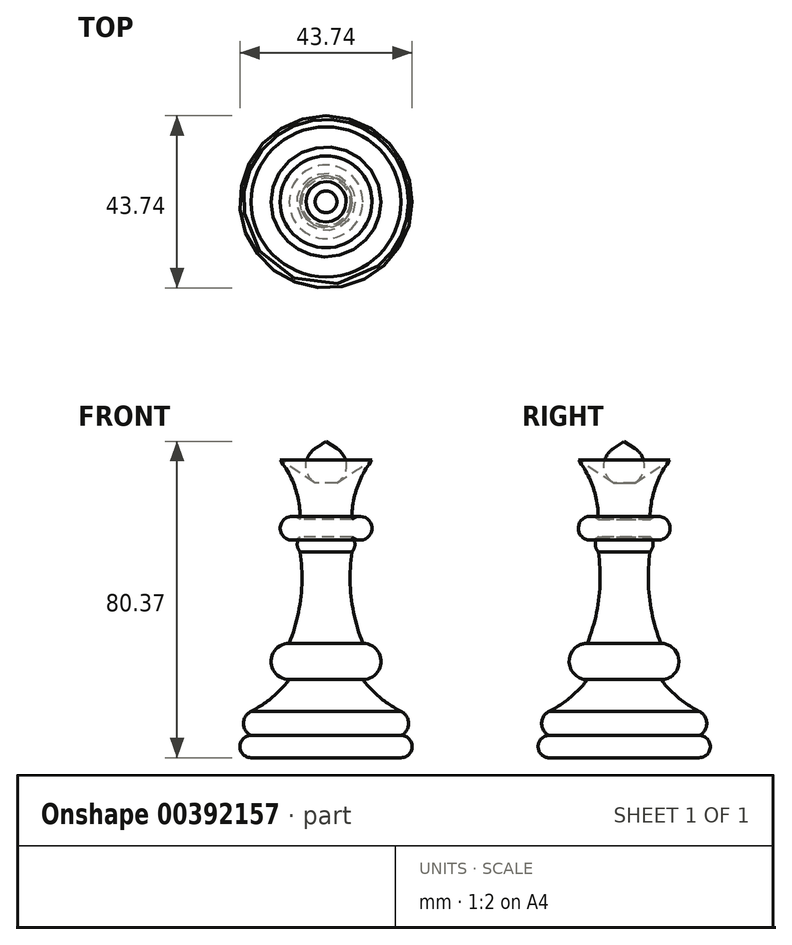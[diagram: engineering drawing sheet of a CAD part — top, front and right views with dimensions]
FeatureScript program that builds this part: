
annotation { "Feature Type Name" : "Feature", "Feature Type Description" : "" }
export const myFeature = defineFeature(function(context is Context, id is Id, definition is map)
    precondition{}
    {
        {
            var Q0;
            Q0=qCreatedBy(makeId("Front.planeOp"),FACE);
            var sketch = newSketch(context, id + "F0", { "sketchPlane" : qUnion([Q0])});
            skLineSegment(sketch, "E0", {"start": v(0, 35.49) * mm, "end": v(0, -34.36) * mm});
            skLineSegment(sketch, "E1", {"start": v(0, -34.36) * mm, "end": v(-19.05, -34.36) * mm});
            skArc(sketch, "E2", {"start": v(-19.05, -28.71) * mm, "mid": v(-21.87, -31.54) * mm, "end": v(-19.05, -34.36) * mm});
            skArc(sketch, "E3", {"start": v(-19.05, -22.58) * mm, "mid": v(-20.97, -25.65) * mm, "end": v(-19.05, -28.71) * mm});
            skArc(sketch, "E4", {"start": v(-19.05, -22.58) * mm, "mid": v(-13.76, -19.09) * mm, "end": v(-9.36, -14.52) * mm});
            skArc(sketch, "E5", {"start": v(-9.36, -5.3) * mm, "mid": v(-13.97, -9.9) * mm, "end": v(-9.36, -14.52) * mm});
            skArc(sketch, "E6", {"start": v(-9.36, -5.3) * mm, "mid": v(-6.43, 6.14) * mm, "end": v(-6.58, 17.94) * mm});
            skArc(sketch, "E7", {"start": v(-6.58, 21.74) * mm, "mid": v(-7.34, 19.84) * mm, "end": v(-6.58, 17.94) * mm});
            skLineSegment(sketch, "E8", {"start": v(0, 40.97) * mm, "end": v(0, 35.49) * mm});
            skPoint(sketch, "E9", {"position": v(-2.77, 35.49) * mm});
            skArc(sketch, "E10", {"start": v(-6.58, 26.13) * mm, "mid": v(-11.67, 23.94) * mm, "end": v(-6.58, 21.74) * mm});
            skArc(sketch, "E11", {"start": v(-6.58, 26.13) * mm, "mid": v(-7.82, 34.15) * mm, "end": v(-11.67, 41.3) * mm});
            skPoint(sketch, "E11.endSnap0", {"position": v(-11.67, 23.94) * mm});
            skLineSegment(sketch, "E12", {"start": v(-11.67, 41.3) * mm, "end": v(-2.77, 35.49) * mm});
            skArc(sketch, "E13", {"start": v(-2.77, 44.2) * mm, "mid": v(-5.13, 39.84) * mm, "end": v(-2.77, 35.49) * mm});
            skLineSegment(sketch, "E14", {"start": v(-2.77, 44.2) * mm, "end": v(0, 46) * mm});
            skLineSegment(sketch, "E15", {"start": v(0, 35.49) * mm, "end": v(0, 46) * mm});
            skSolve(sketch);
        }
        {
            var Q0;
            Q0=qSketchRegion(id+"F0",true);
            var Q1;
            Q1=sQuery(id+"F0.wireOp",EDGE,"E0");
            revolve(context, id + "F1", {"entities" : qUnion([Q0]), "axis" : qUnion([Q1]), "revolveType" : RevolveType.FULL});
        }
    });
